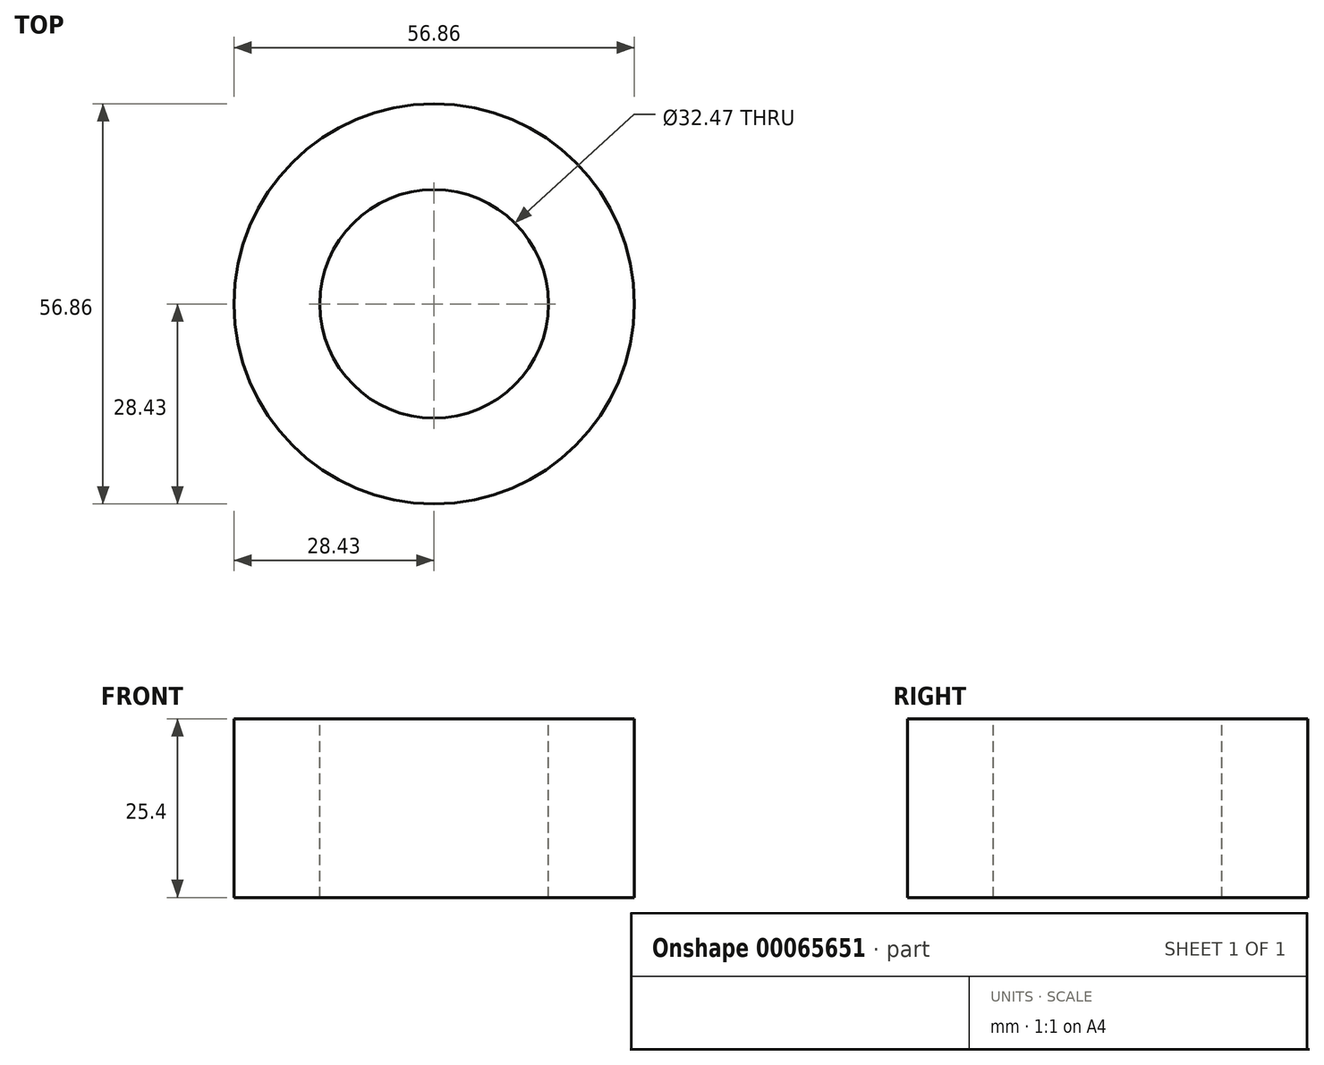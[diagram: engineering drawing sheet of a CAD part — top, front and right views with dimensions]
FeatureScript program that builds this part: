
annotation { "Feature Type Name" : "Feature", "Feature Type Description" : "" }
export const myFeature = defineFeature(function(context is Context, id is Id, definition is map)
    precondition{}
    {
        {
            var Q0;
            Q0=qCreatedBy(makeId("Top.planeOp"),FACE);
            var sketch = newSketch(context, id + "F0", { "sketchPlane" : qUnion([Q0])});
            skCircle(sketch, "E0", {"center": v(0, 0) * mm, "radius": 28.43 * mm});
            skSolve(sketch);
        }
        {
            var Q0;
            Q0=makeQuery(id+"F0.imprint","IMPRINT",FACE,{"disambiguationData":[TD([[makeQuery(id+"F0.imprint","IMPRINT",EDGE,{"derivedFrom":sQuery(id+"F0.wireOp",EDGE,"E0")}),1.0]])]});
            extrude(context, id + "F1", {"entities" : qUnion([Q0]), "depth" : 25.4 * mm});
        }
        {
            var Q0;
            Q0=makeQuery(id+"F1.opExtrude","CAP_FACE",FACE,{"disambiguationData":[OSD([sQuery(id+"F0.wireOp",EDGE,"E0")])],"isStart":false});
            var sketch = newSketch(context, id + "F2", { "sketchPlane" : qUnion([Q0])});
            skSolve(sketch);
        }
        {
            var Q0;
            Q0=makeQuery(id+"F2.imprint","IMPRINT",FACE,{"disambiguationData":[TD([[makeQuery(id+"F2.imprint","IMPRINT",EDGE,{"derivedFrom":makeQuery(id+"F1.opExtrude","CAP_EDGE",EDGE,{"disambiguationData":[OSD([sQuery(id+"F0.wireOp",EDGE,"E0")])],"isStart":false})}),1.0]])]});
            var sketch = newSketch(context, id + "F3", { "sketchPlane" : qUnion([Q0])});
            skCircle(sketch, "E1", {"center": v(0, 0) * mm, "radius": 16.24 * mm});
            skSolve(sketch);
        }
        {
            var Q0;
            Q0=makeQuery(id+"F3.imprint","IMPRINT",FACE,{"disambiguationData":[TD([[makeQuery(id+"F3.imprint","IMPRINT",EDGE,{"derivedFrom":sQuery(id+"F3.wireOp",EDGE,"E1")}),1.0]])]});
            extrude(context, id + "F4", {"entities" : qUnion([Q0]), "operationType" : NewBodyOperationType.REMOVE, "oppositeDirection" : true, "depth" : 86.4 * mm});
        }
    });
